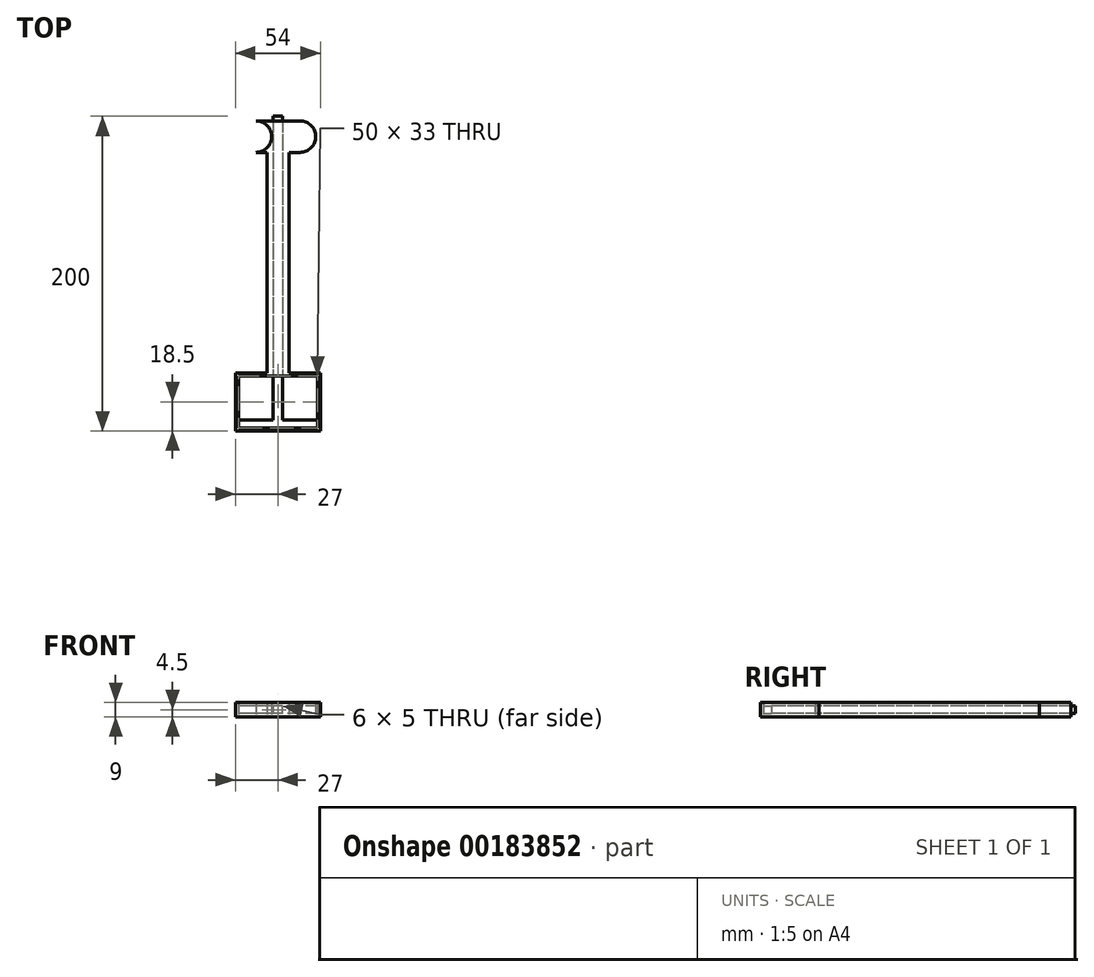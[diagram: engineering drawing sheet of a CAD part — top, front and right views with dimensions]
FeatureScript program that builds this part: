
annotation { "Feature Type Name" : "Feature", "Feature Type Description" : "" }
export const myFeature = defineFeature(function(context is Context, id is Id, definition is map)
    precondition{}
    {
        {
            var Q0;
            Q0=qCreatedBy(makeId("Top.planeOp"),FACE);
            var sketch = newSketch(context, id + "F0", { "sketchPlane" : qUnion([Q0])});
            skLineSegment(sketch, "E0.bottom", {"start": v(0, 13) * mm, "end": v(3, 13) * mm});
            skLineSegment(sketch, "E0.top", {"start": v(0, -180) * mm, "end": v(3, -180) * mm});
            skLineSegment(sketch, "E0.left", {"start": v(0, 13) * mm, "end": v(0, -180) * mm});
            skLineSegment(sketch, "E0.right", {"start": v(3, 13) * mm, "end": v(3, -180) * mm});
            skLineSegment(sketch, "E1", {"start": v(0, 10) * mm, "end": v(3, 10) * mm, "construction": true});
            skArc(sketch, "E2", {"start": v(3, 11.09) * mm, "mid": v(4.04, 10.94) * mm, "end": v(5, 10.5) * mm});
            skLineSegment(sketch, "E3", {"start": v(5, 10.5) * mm, "end": v(5, 10) * mm});
            skArc(sketch, "E4.MirrorCS", {"start": v(3, 8.91) * mm, "mid": v(4.04, 9.06) * mm, "end": v(5, 9.5) * mm});
            skLineSegment(sketch, "E5.MirrorCS", {"start": v(5, 9.5) * mm, "end": v(5, 10) * mm});
            skArc(sketch, "E6.1.0.0", {"start": v(3, 7.89) * mm, "mid": v(4.04, 7.74) * mm, "end": v(5, 7.3) * mm});
            skLineSegment(sketch, "E6.1.0.1", {"start": v(5, 7.3) * mm, "end": v(5, 6.8) * mm});
            skLineSegment(sketch, "E6.1.0.2", {"start": v(5, 6.3) * mm, "end": v(5, 6.8) * mm});
            skArc(sketch, "E6.1.0.3", {"start": v(3, 5.71) * mm, "mid": v(4.04, 5.86) * mm, "end": v(5, 6.3) * mm});
            skArc(sketch, "E6.2.0.0", {"start": v(3, 4.69) * mm, "mid": v(4.04, 4.54) * mm, "end": v(5, 4.1) * mm});
            skLineSegment(sketch, "E6.2.0.1", {"start": v(5, 4.1) * mm, "end": v(5, 3.6) * mm});
            skLineSegment(sketch, "E6.2.0.2", {"start": v(5, 3.1) * mm, "end": v(5, 3.6) * mm});
            skArc(sketch, "E6.2.0.3", {"start": v(3, 2.51) * mm, "mid": v(4.04, 2.66) * mm, "end": v(5, 3.1) * mm});
            skLineSegment(sketch, "E6.direction1", {"start": v(3, 7.39) * mm, "end": v(3, 4.19) * mm, "construction": true});
            skArc(sketch, "E7.0.3.0", {"start": v(3, 1.49) * mm, "mid": v(4.04, 1.34) * mm, "end": v(5, 0.9) * mm});
            skLineSegment(sketch, "E7.4.3.0", {"start": v(5, 0.9) * mm, "end": v(5, 0.4) * mm});
            skLineSegment(sketch, "E7.7.3.0", {"start": v(5, -0.1) * mm, "end": v(5, 0.4) * mm});
            skArc(sketch, "E7.10.3.0", {"start": v(3, -0.69) * mm, "mid": v(4.04, -0.54) * mm, "end": v(5, -0.1) * mm});
            skArc(sketch, "E7.0.4.0", {"start": v(3, -1.71) * mm, "mid": v(4.04, -1.86) * mm, "end": v(5, -2.3) * mm});
            skLineSegment(sketch, "E7.4.4.0", {"start": v(5, -2.3) * mm, "end": v(5, -2.8) * mm});
            skLineSegment(sketch, "E7.7.4.0", {"start": v(5, -3.3) * mm, "end": v(5, -2.8) * mm});
            skArc(sketch, "E7.10.4.0", {"start": v(3, -3.89) * mm, "mid": v(4.04, -3.74) * mm, "end": v(5, -3.3) * mm});
            skArc(sketch, "E7.0.5.0", {"start": v(3, -4.91) * mm, "mid": v(4.04, -5.06) * mm, "end": v(5, -5.5) * mm});
            skLineSegment(sketch, "E7.4.5.0", {"start": v(5, -5.5) * mm, "end": v(5, -6) * mm});
            skLineSegment(sketch, "E7.7.5.0", {"start": v(5, -6.5) * mm, "end": v(5, -6) * mm});
            skArc(sketch, "E7.10.5.0", {"start": v(3, -7.09) * mm, "mid": v(4.04, -6.94) * mm, "end": v(5, -6.5) * mm});
            skArc(sketch, "E7.0.6.0", {"start": v(3, -8.11) * mm, "mid": v(4.04, -8.26) * mm, "end": v(5, -8.7) * mm});
            skLineSegment(sketch, "E7.4.6.0", {"start": v(5, -8.7) * mm, "end": v(5, -9.2) * mm});
            skLineSegment(sketch, "E7.7.6.0", {"start": v(5, -9.7) * mm, "end": v(5, -9.2) * mm});
            skArc(sketch, "E7.10.6.0", {"start": v(3, -10.29) * mm, "mid": v(4.04, -10.14) * mm, "end": v(5, -9.7) * mm});
            skArc(sketch, "E7.0.7.0", {"start": v(3, -11.31) * mm, "mid": v(4.04, -11.46) * mm, "end": v(5, -11.9) * mm});
            skLineSegment(sketch, "E7.4.7.0", {"start": v(5, -11.9) * mm, "end": v(5, -12.4) * mm});
            skLineSegment(sketch, "E7.7.7.0", {"start": v(5, -12.9) * mm, "end": v(5, -12.4) * mm});
            skArc(sketch, "E7.10.7.0", {"start": v(3, -13.49) * mm, "mid": v(4.04, -13.34) * mm, "end": v(5, -12.9) * mm});
            skArc(sketch, "E7.0.8.0", {"start": v(3, -14.51) * mm, "mid": v(4.04, -14.66) * mm, "end": v(5, -15.1) * mm});
            skLineSegment(sketch, "E7.4.8.0", {"start": v(5, -15.1) * mm, "end": v(5, -15.6) * mm});
            skLineSegment(sketch, "E7.7.8.0", {"start": v(5, -16.1) * mm, "end": v(5, -15.6) * mm});
            skArc(sketch, "E7.10.8.0", {"start": v(3, -16.69) * mm, "mid": v(4.04, -16.54) * mm, "end": v(5, -16.1) * mm});
            skArc(sketch, "E7.0.9.0", {"start": v(3, -17.71) * mm, "mid": v(4.04, -17.86) * mm, "end": v(5, -18.3) * mm});
            skLineSegment(sketch, "E7.4.9.0", {"start": v(5, -18.3) * mm, "end": v(5, -18.8) * mm});
            skLineSegment(sketch, "E7.7.9.0", {"start": v(5, -19.3) * mm, "end": v(5, -18.8) * mm});
            skArc(sketch, "E7.10.9.0", {"start": v(3, -19.89) * mm, "mid": v(4.04, -19.74) * mm, "end": v(5, -19.3) * mm});
            skArc(sketch, "E7.0.10.0", {"start": v(3, -20.91) * mm, "mid": v(4.04, -21.06) * mm, "end": v(5, -21.5) * mm});
            skLineSegment(sketch, "E7.4.10.0", {"start": v(5, -21.5) * mm, "end": v(5, -22) * mm});
            skLineSegment(sketch, "E7.7.10.0", {"start": v(5, -22.5) * mm, "end": v(5, -22) * mm});
            skArc(sketch, "E7.10.10.0", {"start": v(3, -23.09) * mm, "mid": v(4.04, -22.94) * mm, "end": v(5, -22.5) * mm});
            skArc(sketch, "E7.0.11.0", {"start": v(3, -24.11) * mm, "mid": v(4.04, -24.26) * mm, "end": v(5, -24.7) * mm});
            skLineSegment(sketch, "E7.4.11.0", {"start": v(5, -24.7) * mm, "end": v(5, -25.2) * mm});
            skLineSegment(sketch, "E7.7.11.0", {"start": v(5, -25.7) * mm, "end": v(5, -25.2) * mm});
            skArc(sketch, "E7.10.11.0", {"start": v(3, -26.29) * mm, "mid": v(4.04, -26.14) * mm, "end": v(5, -25.7) * mm});
            skArc(sketch, "E7.0.12.0", {"start": v(3, -27.31) * mm, "mid": v(4.04, -27.46) * mm, "end": v(5, -27.9) * mm});
            skLineSegment(sketch, "E7.4.12.0", {"start": v(5, -27.9) * mm, "end": v(5, -28.4) * mm});
            skLineSegment(sketch, "E7.7.12.0", {"start": v(5, -28.9) * mm, "end": v(5, -28.4) * mm});
            skArc(sketch, "E7.10.12.0", {"start": v(3, -29.49) * mm, "mid": v(4.04, -29.34) * mm, "end": v(5, -28.9) * mm});
            skArc(sketch, "E7.0.13.0", {"start": v(3, -30.51) * mm, "mid": v(4.04, -30.66) * mm, "end": v(5, -31.1) * mm});
            skLineSegment(sketch, "E7.4.13.0", {"start": v(5, -31.1) * mm, "end": v(5, -31.6) * mm});
            skLineSegment(sketch, "E7.7.13.0", {"start": v(5, -32.1) * mm, "end": v(5, -31.6) * mm});
            skArc(sketch, "E7.10.13.0", {"start": v(3, -32.69) * mm, "mid": v(4.04, -32.54) * mm, "end": v(5, -32.1) * mm});
            skArc(sketch, "E7.0.14.0", {"start": v(3, -33.71) * mm, "mid": v(4.04, -33.86) * mm, "end": v(5, -34.3) * mm});
            skLineSegment(sketch, "E7.4.14.0", {"start": v(5, -34.3) * mm, "end": v(5, -34.8) * mm});
            skLineSegment(sketch, "E7.7.14.0", {"start": v(5, -35.3) * mm, "end": v(5, -34.8) * mm});
            skArc(sketch, "E7.10.14.0", {"start": v(3, -35.89) * mm, "mid": v(4.04, -35.74) * mm, "end": v(5, -35.3) * mm});
            skArc(sketch, "E7.0.15.0", {"start": v(3, -36.91) * mm, "mid": v(4.04, -37.06) * mm, "end": v(5, -37.5) * mm});
            skLineSegment(sketch, "E7.4.15.0", {"start": v(5, -37.5) * mm, "end": v(5, -38) * mm});
            skLineSegment(sketch, "E7.7.15.0", {"start": v(5, -38.5) * mm, "end": v(5, -38) * mm});
            skArc(sketch, "E7.10.15.0", {"start": v(3, -39.09) * mm, "mid": v(4.04, -38.94) * mm, "end": v(5, -38.5) * mm});
            skSolve(sketch);
        }
        {
            var Q0;
            {var subQ18=sQuery(id+"F0.wireOp",EDGE,"E0.bottom");Q0=makeQuery(id+"F0.imprint","IMPRINT",FACE,{"disambiguationData":[TD([[makeQuery(id+"F0.imprint","IMPRINT",EDGE,{"derivedFrom":subQ18}),-1.0]])]});}
            var Q1;
            {var subQ0=sQuery(id+"F0.wireOp",EDGE,"E7.0.15.0");Q1=makeQuery(id+"F0.imprint","IMPRINT",FACE,{"disambiguationData":[TD([[makeQuery(id+"F0.imprint","IMPRINT",EDGE,{"derivedFrom":subQ0}),-1.0]])]});}
            var Q2;
            {var subQ0=sQuery(id+"F0.wireOp",EDGE,"E7.0.14.0");Q2=makeQuery(id+"F0.imprint","IMPRINT",FACE,{"disambiguationData":[TD([[makeQuery(id+"F0.imprint","IMPRINT",EDGE,{"derivedFrom":subQ0}),-1.0]])]});}
            var Q3;
            {var subQ0=sQuery(id+"F0.wireOp",EDGE,"E7.0.13.0");Q3=makeQuery(id+"F0.imprint","IMPRINT",FACE,{"disambiguationData":[TD([[makeQuery(id+"F0.imprint","IMPRINT",EDGE,{"derivedFrom":subQ0}),-1.0]])]});}
            var Q4;
            {var subQ0=sQuery(id+"F0.wireOp",EDGE,"E7.0.12.0");Q4=makeQuery(id+"F0.imprint","IMPRINT",FACE,{"disambiguationData":[TD([[makeQuery(id+"F0.imprint","IMPRINT",EDGE,{"derivedFrom":subQ0}),-1.0]])]});}
            var Q5;
            {var subQ1=sQuery(id+"F0.wireOp",EDGE,"E7.0.11.0");Q5=makeQuery(id+"F0.imprint","IMPRINT",FACE,{"disambiguationData":[TD([[makeQuery(id+"F0.imprint","IMPRINT",EDGE,{"derivedFrom":subQ1}),-1.0]])]});}
            var Q6;
            {var subQ0=sQuery(id+"F0.wireOp",EDGE,"E7.0.10.0");Q6=makeQuery(id+"F0.imprint","IMPRINT",FACE,{"disambiguationData":[TD([[makeQuery(id+"F0.imprint","IMPRINT",EDGE,{"derivedFrom":subQ0}),-1.0]])]});}
            var Q7;
            {var subQ0=sQuery(id+"F0.wireOp",EDGE,"E7.0.9.0");Q7=makeQuery(id+"F0.imprint","IMPRINT",FACE,{"disambiguationData":[TD([[makeQuery(id+"F0.imprint","IMPRINT",EDGE,{"derivedFrom":subQ0}),-1.0]])]});}
            var Q8;
            {var subQ0=sQuery(id+"F0.wireOp",EDGE,"E7.0.8.0");Q8=makeQuery(id+"F0.imprint","IMPRINT",FACE,{"disambiguationData":[TD([[makeQuery(id+"F0.imprint","IMPRINT",EDGE,{"derivedFrom":subQ0}),-1.0]])]});}
            var Q9;
            {var subQ0=sQuery(id+"F0.wireOp",EDGE,"E7.0.7.0");Q9=makeQuery(id+"F0.imprint","IMPRINT",FACE,{"disambiguationData":[TD([[makeQuery(id+"F0.imprint","IMPRINT",EDGE,{"derivedFrom":subQ0}),-1.0]])]});}
            var Q10;
            {var subQ0=sQuery(id+"F0.wireOp",EDGE,"E7.0.6.0");Q10=makeQuery(id+"F0.imprint","IMPRINT",FACE,{"disambiguationData":[TD([[makeQuery(id+"F0.imprint","IMPRINT",EDGE,{"derivedFrom":subQ0}),-1.0]])]});}
            var Q11;
            {var subQ0=sQuery(id+"F0.wireOp",EDGE,"E7.0.5.0");Q11=makeQuery(id+"F0.imprint","IMPRINT",FACE,{"disambiguationData":[TD([[makeQuery(id+"F0.imprint","IMPRINT",EDGE,{"derivedFrom":subQ0}),-1.0]])]});}
            var Q12;
            {var subQ0=sQuery(id+"F0.wireOp",EDGE,"E7.0.4.0");Q12=makeQuery(id+"F0.imprint","IMPRINT",FACE,{"disambiguationData":[TD([[makeQuery(id+"F0.imprint","IMPRINT",EDGE,{"derivedFrom":subQ0}),-1.0]])]});}
            var Q13;
            {var subQ0=sQuery(id+"F0.wireOp",EDGE,"E7.0.3.0");Q13=makeQuery(id+"F0.imprint","IMPRINT",FACE,{"disambiguationData":[TD([[makeQuery(id+"F0.imprint","IMPRINT",EDGE,{"derivedFrom":subQ0}),-1.0]])]});}
            var Q14;
            {var subQ0=sQuery(id+"F0.wireOp",EDGE,"E6.2.0.0");Q14=makeQuery(id+"F0.imprint","IMPRINT",FACE,{"disambiguationData":[TD([[makeQuery(id+"F0.imprint","IMPRINT",EDGE,{"derivedFrom":subQ0}),-1.0]])]});}
            var Q15;
            {var subQ0=sQuery(id+"F0.wireOp",EDGE,"E6.1.0.0");Q15=makeQuery(id+"F0.imprint","IMPRINT",FACE,{"disambiguationData":[TD([[makeQuery(id+"F0.imprint","IMPRINT",EDGE,{"derivedFrom":subQ0}),-1.0]])]});}
            var Q16;
            {var subQ1=sQuery(id+"F0.wireOp",EDGE,"E2");Q16=makeQuery(id+"F0.imprint","IMPRINT",FACE,{"disambiguationData":[TD([[makeQuery(id+"F0.imprint","IMPRINT",EDGE,{"derivedFrom":subQ1}),-1.0]])]});}
            extrude(context, id + "F1", {"entities" : qUnion([Q0, Q1, Q2, Q3, Q4, Q5, Q6, Q7, Q8, Q9, Q10, Q11, Q12, Q13, Q14, Q15, Q16]), "depth" : 5 * mm});
        }
        {
            var Q0;
            Q0=makeQuery(id+"F1.opExtrude","SWEPT_BODY",BODY,{"disambiguationData":[OSD([sQuery(id+"F0.wireOp",EDGE,"E0.bottom"),sQuery(id+"F0.wireOp",EDGE,"E0.top"),sQuery(id+"F0.wireOp",EDGE,"E0.left"),sQuery(id+"F0.wireOp",EDGE,"E0.right"),sQuery(id+"F0.wireOp",EDGE,"E2"),sQuery(id+"F0.wireOp",EDGE,"E3"),sQuery(id+"F0.wireOp",EDGE,"E4.MirrorCS"),sQuery(id+"F0.wireOp",EDGE,"E5.MirrorCS"),sQuery(id+"F0.wireOp",EDGE,"E6.1.0.0"),sQuery(id+"F0.wireOp",EDGE,"E6.1.0.1"),sQuery(id+"F0.wireOp",EDGE,"E6.1.0.2"),sQuery(id+"F0.wireOp",EDGE,"E6.1.0.3"),sQuery(id+"F0.wireOp",EDGE,"E6.2.0.0"),sQuery(id+"F0.wireOp",EDGE,"E6.2.0.1"),sQuery(id+"F0.wireOp",EDGE,"E6.2.0.2"),sQuery(id+"F0.wireOp",EDGE,"E6.2.0.3"),sQuery(id+"F0.wireOp",EDGE,"E7.0.3.0"),sQuery(id+"F0.wireOp",EDGE,"E7.4.3.0"),sQuery(id+"F0.wireOp",EDGE,"E7.7.3.0"),sQuery(id+"F0.wireOp",EDGE,"E7.10.3.0"),sQuery(id+"F0.wireOp",EDGE,"E7.0.4.0"),sQuery(id+"F0.wireOp",EDGE,"E7.4.4.0"),sQuery(id+"F0.wireOp",EDGE,"E7.7.4.0"),sQuery(id+"F0.wireOp",EDGE,"E7.10.4.0"),sQuery(id+"F0.wireOp",EDGE,"E7.0.5.0"),sQuery(id+"F0.wireOp",EDGE,"E7.4.5.0"),sQuery(id+"F0.wireOp",EDGE,"E7.7.5.0"),sQuery(id+"F0.wireOp",EDGE,"E7.10.5.0"),sQuery(id+"F0.wireOp",EDGE,"E7.0.6.0"),sQuery(id+"F0.wireOp",EDGE,"E7.4.6.0"),sQuery(id+"F0.wireOp",EDGE,"E7.7.6.0"),sQuery(id+"F0.wireOp",EDGE,"E7.10.6.0"),sQuery(id+"F0.wireOp",EDGE,"E7.0.7.0"),sQuery(id+"F0.wireOp",EDGE,"E7.4.7.0"),sQuery(id+"F0.wireOp",EDGE,"E7.7.7.0"),sQuery(id+"F0.wireOp",EDGE,"E7.10.7.0"),sQuery(id+"F0.wireOp",EDGE,"E7.0.8.0"),sQuery(id+"F0.wireOp",EDGE,"E7.4.8.0"),sQuery(id+"F0.wireOp",EDGE,"E7.7.8.0"),sQuery(id+"F0.wireOp",EDGE,"E7.10.8.0"),sQuery(id+"F0.wireOp",EDGE,"E7.0.9.0"),sQuery(id+"F0.wireOp",EDGE,"E7.4.9.0"),sQuery(id+"F0.wireOp",EDGE,"E7.7.9.0"),sQuery(id+"F0.wireOp",EDGE,"E7.10.9.0"),sQuery(id+"F0.wireOp",EDGE,"E7.0.10.0"),sQuery(id+"F0.wireOp",EDGE,"E7.4.10.0"),sQuery(id+"F0.wireOp",EDGE,"E7.7.10.0"),sQuery(id+"F0.wireOp",EDGE,"E7.10.10.0"),sQuery(id+"F0.wireOp",EDGE,"E7.0.11.0"),sQuery(id+"F0.wireOp",EDGE,"E7.4.11.0"),sQuery(id+"F0.wireOp",EDGE,"E7.7.11.0"),sQuery(id+"F0.wireOp",EDGE,"E7.10.11.0"),sQuery(id+"F0.wireOp",EDGE,"E7.0.12.0"),sQuery(id+"F0.wireOp",EDGE,"E7.4.12.0"),sQuery(id+"F0.wireOp",EDGE,"E7.7.12.0"),sQuery(id+"F0.wireOp",EDGE,"E7.10.12.0"),sQuery(id+"F0.wireOp",EDGE,"E7.0.13.0"),sQuery(id+"F0.wireOp",EDGE,"E7.4.13.0"),sQuery(id+"F0.wireOp",EDGE,"E7.7.13.0"),sQuery(id+"F0.wireOp",EDGE,"E7.10.13.0"),sQuery(id+"F0.wireOp",EDGE,"E7.0.14.0"),sQuery(id+"F0.wireOp",EDGE,"E7.4.14.0"),sQuery(id+"F0.wireOp",EDGE,"E7.7.14.0"),sQuery(id+"F0.wireOp",EDGE,"E7.10.14.0"),sQuery(id+"F0.wireOp",EDGE,"E7.0.15.0"),sQuery(id+"F0.wireOp",EDGE,"E7.4.15.0"),sQuery(id+"F0.wireOp",EDGE,"E7.7.15.0"),sQuery(id+"F0.wireOp",EDGE,"E7.10.15.0")])]});
            var Q1;
            Q1=makeQuery(id+"F1.opExtrude","SWEPT_FACE",FACE,{"disambiguationData":[OSD([sQuery(id+"F0.wireOp",EDGE,"E0.left")])]});
            mirror(context, id + "F2", {"operationType" : NewBodyOperationType.ADD, "entities" : qUnion([Q0]), "mirrorPlane" : qUnion([Q1])});
        }
        {
            var Q0;
            {var subQ0=makeQuery(id+"F1.opExtrude","SWEPT_FACE",FACE,{"disambiguationData":[OSD([sQuery(id+"F0.wireOp",EDGE,"E0.top")])]});Q0=makeQuery(id+"F2.boolean.opBoolean","MERGE",FACE,{"derivedFrom":[subQ0,makeQuery(id+"F2.opPattern","COPY",FACE,{"derivedFrom":subQ0,"instanceName":"1"})]});}
            var sketch = newSketch(context, id + "F3", { "sketchPlane" : qUnion([Q0])});
            skLineSegment(sketch, "E8.bottom", {"start": v(25, 5) * mm, "end": v(-25, 5) * mm});
            skLineSegment(sketch, "E8.top", {"start": v(25, 0) * mm, "end": v(-25, 0) * mm});
            skLineSegment(sketch, "E8.left", {"start": v(25, 5) * mm, "end": v(25, 0) * mm});
            skLineSegment(sketch, "E8.right", {"start": v(-25, 5) * mm, "end": v(-25, 0) * mm});
            skPoint(sketch, "E8.middle", {"position": v(0, 2.5) * mm});
            skPoint(sketch, "E8.middle.positionSnap0", {"position": v(0, 0) * mm});
            skPoint(sketch, "E8.middle.positionSnap1", {"position": v(3, 2.5) * mm});
            skPoint(sketch, "E8.centerSnap0", {"position": v(0, 0) * mm});
            skPoint(sketch, "E8.centerSnap1", {"position": v(3, 2.5) * mm});
            skSolve(sketch);
        }
        {
            var Q0;
            {var subQ2=sQuery(id+"F3.wireOp",EDGE,"E8.left");Q0=makeQuery(id+"F3.imprint","IMPRINT",FACE,{"disambiguationData":[TD([[makeQuery(id+"F3.imprint","IMPRINT",EDGE,{"derivedFrom":subQ2}),-1.0]])]});}
            var Q1;
            {var subQ1=makeQuery(id+"F1.opExtrude","SWEPT_EDGE",EDGE,{"disambiguationData":[OSD([sQuery(id+"F0.wireOp",EDGE,"E0.top"),sQuery(id+"F0.wireOp",EDGE,"E0.right")])]});Q1=makeQuery(id+"F3.imprint","IMPRINT",FACE,{"disambiguationData":[TD([[makeQuery(id+"F3.imprint","IMPRINT",EDGE,{"derivedFrom":subQ1}),-1.0]])]});}
            var Q2;
            {var subQ2=sQuery(id+"F3.wireOp",EDGE,"E8.right");Q2=makeQuery(id+"F3.imprint","IMPRINT",FACE,{"disambiguationData":[TD([[makeQuery(id+"F3.imprint","IMPRINT",EDGE,{"derivedFrom":subQ2}),1.0]])]});}
            extrude(context, id + "F4", {"entities" : qUnion([Q0, Q1, Q2]), "operationType" : NewBodyOperationType.ADD, "depth" : 5 * mm});
        }
        {
            var Q0;
            Q0=qCreatedBy(makeId("Top.planeOp"),FACE);
            var sketch = newSketch(context, id + "F5", { "sketchPlane" : qUnion([Q0])});
            skCircle(sketch, "E9", {"center": v(14, 0) * mm, "radius": 10 * mm});
            skLineSegment(sketch, "E10", {"start": v(14, 10) * mm, "end": v(0, 10) * mm});
            skLineSegment(sketch, "E11", {"start": v(14, -10) * mm, "end": v(7, -10) * mm});
            skLineSegment(sketch, "E12", {"start": v(7, -10) * mm, "end": v(7, -150) * mm});
            skLineSegment(sketch, "E13", {"start": v(7, -150) * mm, "end": v(27, -150) * mm});
            skLineSegment(sketch, "E14", {"start": v(27, -150) * mm, "end": v(27, -187) * mm});
            skLineSegment(sketch, "E15", {"start": v(27, -187) * mm, "end": v(0, -187) * mm});
            skLineSegment(sketch, "E16.MirrorCS", {"start": v(-14, 10) * mm, "end": v(0, 10) * mm});
            skCircle(sketch, "E17.MirrorC", {"center": v(-14, 0) * mm, "radius": 10 * mm});
            skLineSegment(sketch, "E18.MirrorCS", {"start": v(-14, -10) * mm, "end": v(-7, -10) * mm});
            skLineSegment(sketch, "E19.MirrorCS", {"start": v(-7, -10) * mm, "end": v(-7, -150) * mm});
            skLineSegment(sketch, "E20.MirrorCS", {"start": v(-7, -150) * mm, "end": v(-27, -150) * mm});
            skLineSegment(sketch, "E21.MirrorCS", {"start": v(-27, -150) * mm, "end": v(-27, -187) * mm});
            skLineSegment(sketch, "E22.MirrorCS", {"start": v(-27, -187) * mm, "end": v(0, -187) * mm});
            skLineSegment(sketch, "E23.bottom", {"start": v(25, -185) * mm, "end": v(-25, -185) * mm});
            skLineSegment(sketch, "E23.top", {"start": v(25, -152) * mm, "end": v(-25, -152) * mm});
            skLineSegment(sketch, "E23.left", {"start": v(25, -185) * mm, "end": v(25, -152) * mm});
            skLineSegment(sketch, "E23.right", {"start": v(-25, -185) * mm, "end": v(-25, -152) * mm});
            skPoint(sketch, "E23.middle", {"position": v(0, -168.5) * mm});
            skSolve(sketch);
        }
        {
            var Q0;
            {var subQ3=sQuery(id+"F5.wireOp",EDGE,"E10");Q0=makeQuery(id+"F5.imprint","IMPRINT",FACE,{"disambiguationData":[TD([[makeQuery(id+"F5.imprint","IMPRINT",EDGE,{"derivedFrom":subQ3}),1.0]])]});}
            var Q1;
            {var subQ0=sQuery(id+"F5.wireOp",EDGE,"E17.MirrorC");var subQ1=makeQuery(id+"F5.imprint","INTERSECT",VERTEX,{"derivedFrom":[sQuery(id+"F5.wireOp",EDGE,"E16.MirrorCS"),subQ0]});Q1=makeQuery(id+"F5.imprint","IMPRINT",FACE,{"disambiguationData":[TD([[makeQuery(id+"F5.imprint","IMPRINT",EDGE,{"disambiguationData":[TD([[subQ1,-1.0]])],"derivedFrom":subQ0}),-1.0]])]});}
            var Q2;
            {var subQ0=sQuery(id+"F5.wireOp",EDGE,"E9");var subQ1=makeQuery(id+"F5.imprint","INTERSECT",VERTEX,{"derivedFrom":[subQ0,sQuery(id+"F5.wireOp",EDGE,"E10")]});Q2=makeQuery(id+"F5.imprint","IMPRINT",FACE,{"disambiguationData":[TD([[makeQuery(id+"F5.imprint","IMPRINT",EDGE,{"disambiguationData":[TD([[subQ1,-1.0]])],"derivedFrom":subQ0}),1.0]])]});}
            extrude(context, id + "F6", {"entities" : qUnion([Q0, Q1, Q2]), "depth" : 7 * mm, "hasSecondDirection" : true, "secondDirectionOppositeDirection" : true, "secondDirectionDepth" : 2 * mm});
        }
        {
            var Q0;
            Q0=makeQuery(id+"F1.opExtrude","SWEPT_BODY",BODY,{"disambiguationData":[OSD([sQuery(id+"F0.wireOp",EDGE,"E0.bottom"),sQuery(id+"F0.wireOp",EDGE,"E0.top"),sQuery(id+"F0.wireOp",EDGE,"E0.left"),sQuery(id+"F0.wireOp",EDGE,"E0.right"),sQuery(id+"F0.wireOp",EDGE,"E2"),sQuery(id+"F0.wireOp",EDGE,"E3"),sQuery(id+"F0.wireOp",EDGE,"E4.MirrorCS"),sQuery(id+"F0.wireOp",EDGE,"E5.MirrorCS"),sQuery(id+"F0.wireOp",EDGE,"E6.1.0.0"),sQuery(id+"F0.wireOp",EDGE,"E6.1.0.1"),sQuery(id+"F0.wireOp",EDGE,"E6.1.0.2"),sQuery(id+"F0.wireOp",EDGE,"E6.1.0.3"),sQuery(id+"F0.wireOp",EDGE,"E6.2.0.0"),sQuery(id+"F0.wireOp",EDGE,"E6.2.0.1"),sQuery(id+"F0.wireOp",EDGE,"E6.2.0.2"),sQuery(id+"F0.wireOp",EDGE,"E6.2.0.3"),sQuery(id+"F0.wireOp",EDGE,"E7.0.3.0"),sQuery(id+"F0.wireOp",EDGE,"E7.4.3.0"),sQuery(id+"F0.wireOp",EDGE,"E7.7.3.0"),sQuery(id+"F0.wireOp",EDGE,"E7.10.3.0"),sQuery(id+"F0.wireOp",EDGE,"E7.0.4.0"),sQuery(id+"F0.wireOp",EDGE,"E7.4.4.0"),sQuery(id+"F0.wireOp",EDGE,"E7.7.4.0"),sQuery(id+"F0.wireOp",EDGE,"E7.10.4.0"),sQuery(id+"F0.wireOp",EDGE,"E7.0.5.0"),sQuery(id+"F0.wireOp",EDGE,"E7.4.5.0"),sQuery(id+"F0.wireOp",EDGE,"E7.7.5.0"),sQuery(id+"F0.wireOp",EDGE,"E7.10.5.0"),sQuery(id+"F0.wireOp",EDGE,"E7.0.6.0"),sQuery(id+"F0.wireOp",EDGE,"E7.4.6.0"),sQuery(id+"F0.wireOp",EDGE,"E7.7.6.0"),sQuery(id+"F0.wireOp",EDGE,"E7.10.6.0"),sQuery(id+"F0.wireOp",EDGE,"E7.0.7.0"),sQuery(id+"F0.wireOp",EDGE,"E7.4.7.0"),sQuery(id+"F0.wireOp",EDGE,"E7.7.7.0"),sQuery(id+"F0.wireOp",EDGE,"E7.10.7.0"),sQuery(id+"F0.wireOp",EDGE,"E7.0.8.0"),sQuery(id+"F0.wireOp",EDGE,"E7.4.8.0"),sQuery(id+"F0.wireOp",EDGE,"E7.7.8.0"),sQuery(id+"F0.wireOp",EDGE,"E7.10.8.0"),sQuery(id+"F0.wireOp",EDGE,"E7.0.9.0"),sQuery(id+"F0.wireOp",EDGE,"E7.4.9.0"),sQuery(id+"F0.wireOp",EDGE,"E7.7.9.0"),sQuery(id+"F0.wireOp",EDGE,"E7.10.9.0"),sQuery(id+"F0.wireOp",EDGE,"E7.0.10.0"),sQuery(id+"F0.wireOp",EDGE,"E7.4.10.0"),sQuery(id+"F0.wireOp",EDGE,"E7.7.10.0"),sQuery(id+"F0.wireOp",EDGE,"E7.10.10.0"),sQuery(id+"F0.wireOp",EDGE,"E7.0.11.0"),sQuery(id+"F0.wireOp",EDGE,"E7.4.11.0"),sQuery(id+"F0.wireOp",EDGE,"E7.7.11.0"),sQuery(id+"F0.wireOp",EDGE,"E7.10.11.0"),sQuery(id+"F0.wireOp",EDGE,"E7.0.12.0"),sQuery(id+"F0.wireOp",EDGE,"E7.4.12.0"),sQuery(id+"F0.wireOp",EDGE,"E7.7.12.0"),sQuery(id+"F0.wireOp",EDGE,"E7.10.12.0"),sQuery(id+"F0.wireOp",EDGE,"E7.0.13.0"),sQuery(id+"F0.wireOp",EDGE,"E7.4.13.0"),sQuery(id+"F0.wireOp",EDGE,"E7.7.13.0"),sQuery(id+"F0.wireOp",EDGE,"E7.10.13.0"),sQuery(id+"F0.wireOp",EDGE,"E7.0.14.0"),sQuery(id+"F0.wireOp",EDGE,"E7.4.14.0"),sQuery(id+"F0.wireOp",EDGE,"E7.7.14.0"),sQuery(id+"F0.wireOp",EDGE,"E7.10.14.0"),sQuery(id+"F0.wireOp",EDGE,"E7.0.15.0"),sQuery(id+"F0.wireOp",EDGE,"E7.4.15.0"),sQuery(id+"F0.wireOp",EDGE,"E7.7.15.0"),sQuery(id+"F0.wireOp",EDGE,"E7.10.15.0")])]});
            var Q1;
            Q1=makeQuery(id+"F6.opExtrude","SWEPT_BODY",BODY,{"disambiguationData":[OSD([sQuery(id+"F5.wireOp",EDGE,"E9"),sQuery(id+"F5.wireOp",EDGE,"E10"),sQuery(id+"F5.wireOp",EDGE,"E11"),sQuery(id+"F5.wireOp",EDGE,"E12"),sQuery(id+"F5.wireOp",EDGE,"E13"),sQuery(id+"F5.wireOp",EDGE,"E14"),sQuery(id+"F5.wireOp",EDGE,"E15"),sQuery(id+"F5.wireOp",EDGE,"E16.MirrorCS"),sQuery(id+"F5.wireOp",EDGE,"E17.MirrorC"),sQuery(id+"F5.wireOp",EDGE,"E18.MirrorCS"),sQuery(id+"F5.wireOp",EDGE,"E19.MirrorCS"),sQuery(id+"F5.wireOp",EDGE,"E20.MirrorCS"),sQuery(id+"F5.wireOp",EDGE,"E21.MirrorCS"),sQuery(id+"F5.wireOp",EDGE,"E22.MirrorCS"),sQuery(id+"F5.wireOp",EDGE,"E23.bottom"),sQuery(id+"F5.wireOp",EDGE,"E23.top"),sQuery(id+"F5.wireOp",EDGE,"E23.left"),sQuery(id+"F5.wireOp",EDGE,"E23.right")])]});
            booleanBodies(context, id + "F7", {"operationType" : BooleanOperationType.SUBTRACTION, "tools" : qUnion([Q0]), "targets" : qUnion([Q1]), "keepTools" : true});
        }
    });
